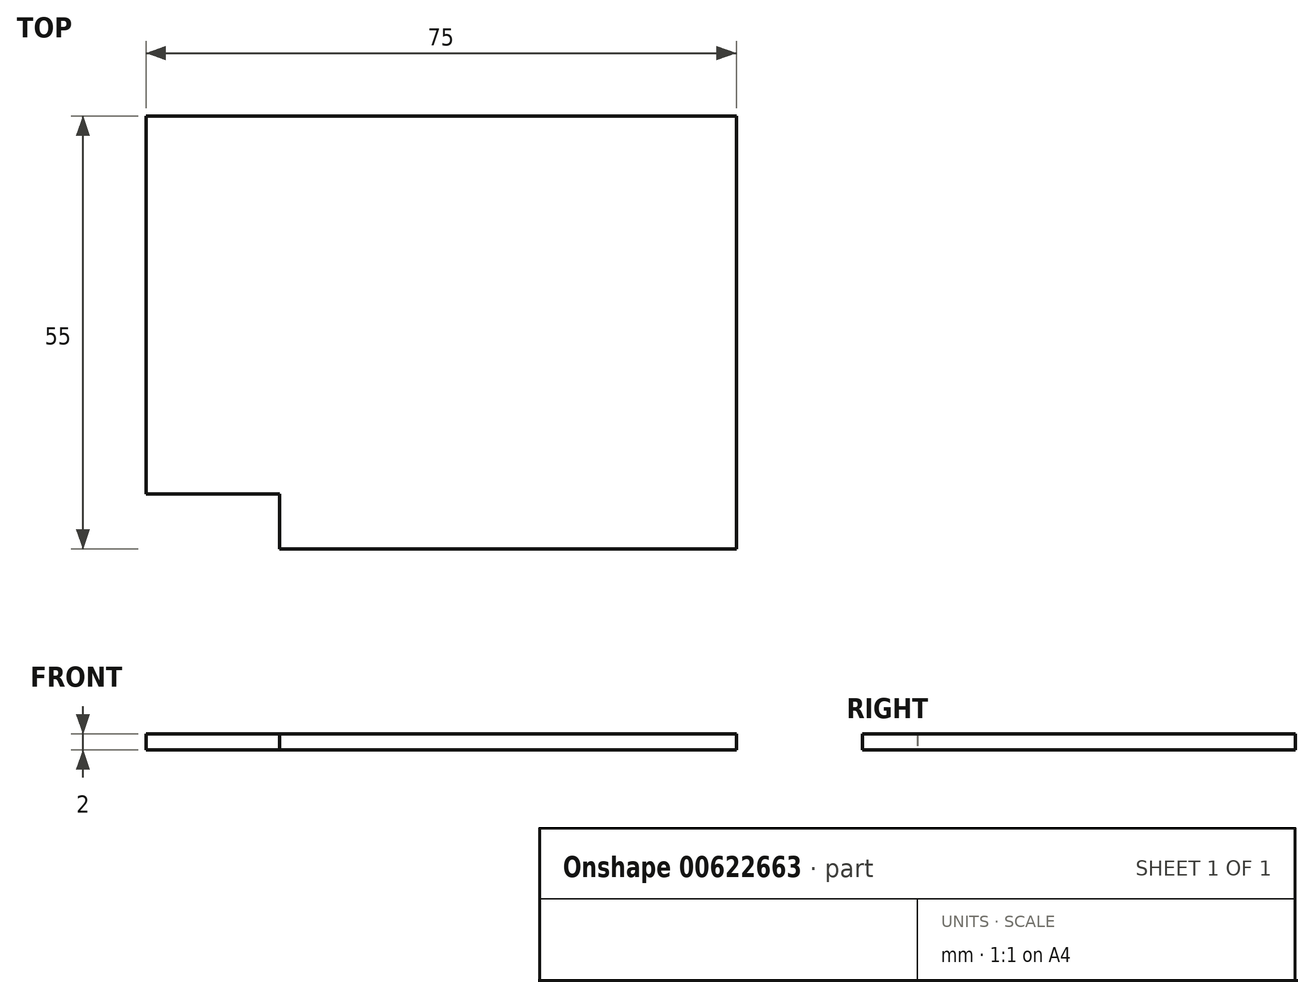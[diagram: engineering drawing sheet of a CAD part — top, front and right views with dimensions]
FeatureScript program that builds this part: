
annotation { "Feature Type Name" : "Feature", "Feature Type Description" : "" }
export const myFeature = defineFeature(function(context is Context, id is Id, definition is map)
    precondition{}
    {
        {
            var Q0;
            Q0=qCreatedBy(makeId("Top.planeOp"),FACE);
            var sketch = newSketch(context, id + "F0", { "sketchPlane" : qUnion([Q0])});
            skLineSegment(sketch, "E0.bottom", {"start": v(37.5, -27.5) * mm, "end": v(-37.5, -27.5) * mm});
            skLineSegment(sketch, "E0.top", {"start": v(37.5, 27.5) * mm, "end": v(-37.5, 27.5) * mm});
            skLineSegment(sketch, "E0.left", {"start": v(37.5, -27.5) * mm, "end": v(37.5, 27.5) * mm});
            skLineSegment(sketch, "E0.right", {"start": v(-37.5, -27.5) * mm, "end": v(-37.5, 27.5) * mm});
            skPoint(sketch, "E0.middle", {"position": v(0, 0) * mm});
            skLineSegment(sketch, "E1.bottom", {"start": v(-20.5, -20.5) * mm, "end": v(-35.5, -20.5) * mm});
            skLineSegment(sketch, "E1.top", {"start": v(-20.5, -25.5) * mm, "end": v(-35.5, -25.5) * mm});
            skLineSegment(sketch, "E1.left", {"start": v(-20.5, -20.5) * mm, "end": v(-20.5, -25.5) * mm});
            skLineSegment(sketch, "E1.right", {"start": v(-35.5, -20.5) * mm, "end": v(-35.5, -25.5) * mm});
            skPoint(sketch, "E1.middle", {"position": v(-28, -23) * mm});
            skLineSegment(sketch, "E2", {"start": v(-35.5, -25.5) * mm, "end": v(-35.5, -27.5) * mm});
            skLineSegment(sketch, "E3", {"start": v(-35.5, -27.5) * mm, "end": v(-20.5, -27.5) * mm});
            skLineSegment(sketch, "E4", {"start": v(-20.5, -27.5) * mm, "end": v(-20.5, -25.5) * mm});
            skLineSegment(sketch, "E5", {"start": v(-35.5, -20.5) * mm, "end": v(-37.5, -20.5) * mm});
            skSolve(sketch);
        }
        {
            var Q0;
            {var subQ1=sQuery(id+"F0.wireOp",EDGE,"E0.top");Q0=makeQuery(id+"F0.imprint","IMPRINT",FACE,{"disambiguationData":[TD([[makeQuery(id+"F0.imprint","IMPRINT",EDGE,{"derivedFrom":subQ1}),1.0]])]});}
            extrude(context, id + "F1", {"entities" : qUnion([Q0]), "depth" : 2 * mm, "offsetDistance" : 25 * mm});
        }
    });
